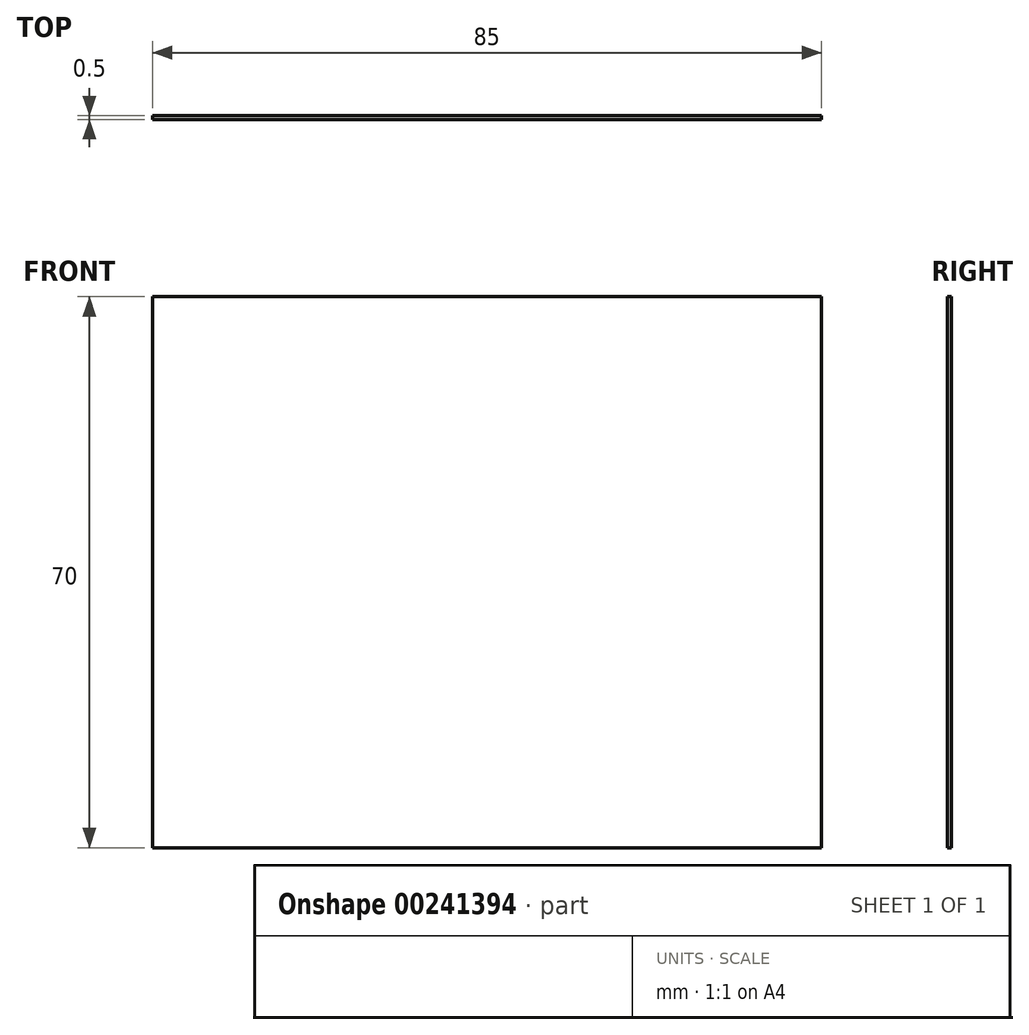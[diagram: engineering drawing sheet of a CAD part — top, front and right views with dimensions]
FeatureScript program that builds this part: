
annotation { "Feature Type Name" : "Feature", "Feature Type Description" : "" }
export const myFeature = defineFeature(function(context is Context, id is Id, definition is map)
    precondition{}
    {
        {
            var Q0;
            Q0=qCreatedBy(makeId("Front.planeOp"),FACE);
            var sketch = newSketch(context, id + "F0", { "sketchPlane" : qUnion([Q0])});
            skLineSegment(sketch, "E0.bottom", {"start": v(-42.5, 35) * mm, "end": v(42.5, 35) * mm});
            skLineSegment(sketch, "E0.top", {"start": v(-42.5, -35) * mm, "end": v(42.5, -35) * mm});
            skLineSegment(sketch, "E0.left", {"start": v(-42.5, 35) * mm, "end": v(-42.5, -35) * mm});
            skLineSegment(sketch, "E0.right", {"start": v(42.5, 35) * mm, "end": v(42.5, -35) * mm});
            skPoint(sketch, "E0.middle", {"position": v(0, 0) * mm});
            skSolve(sketch);
        }
        {
            var Q0;
            Q0 = qSketchRegion(id + "F0", true);
            extrude(context, id + "F1", {"entities" : qUnion([Q0]), "depth" : .5 * mm});
        }
    });
